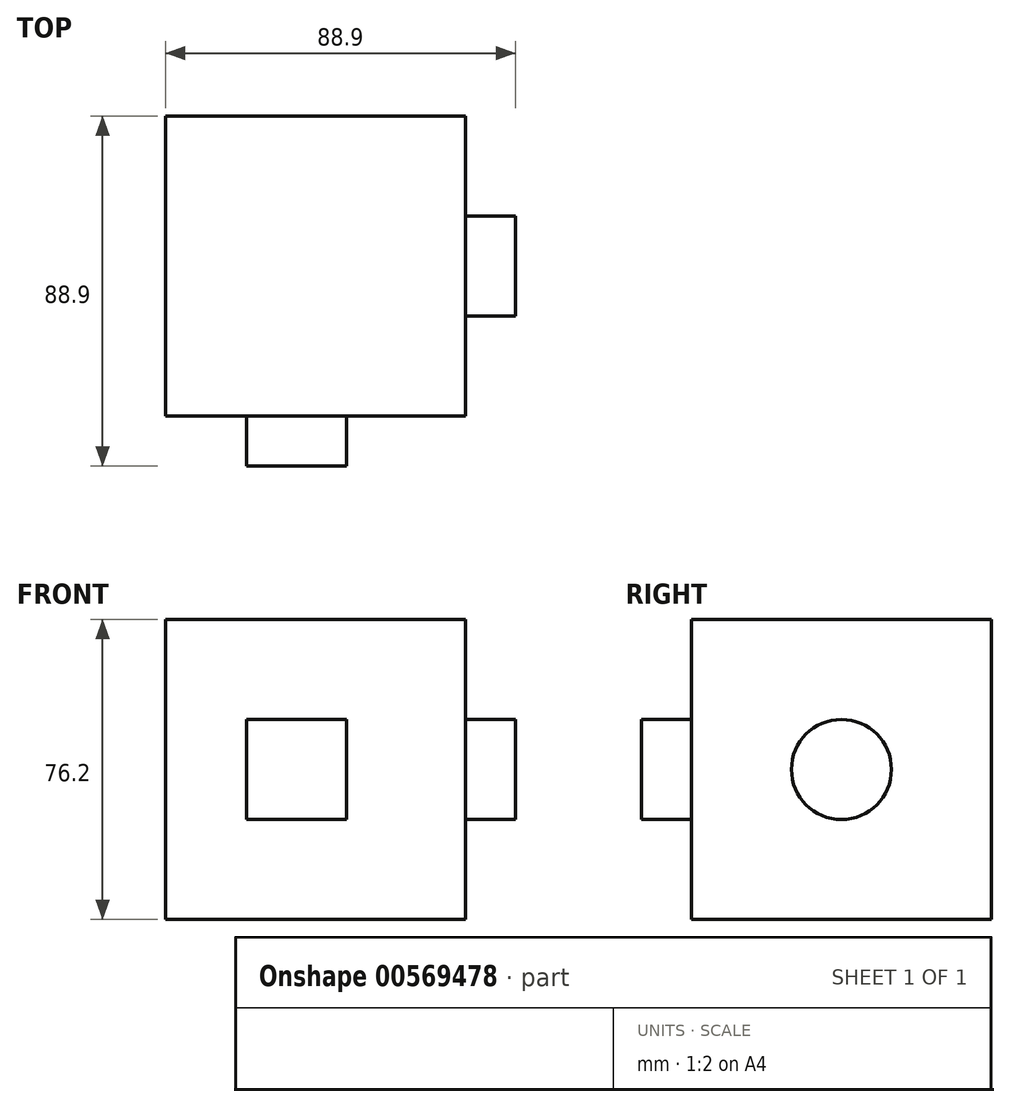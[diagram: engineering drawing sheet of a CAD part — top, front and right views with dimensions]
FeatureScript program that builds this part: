
annotation { "Feature Type Name" : "Feature", "Feature Type Description" : "" }
export const myFeature = defineFeature(function(context is Context, id is Id, definition is map)
    precondition{}
    {
        {
            var Q0;
            Q0=qCreatedBy(makeId("Front.planeOp"),FACE);
            var sketch = newSketch(context, id + "F0", { "sketchPlane" : qUnion([Q0])});
            skLineSegment(sketch, "E0.bottom", {"start": v(-1.68, 93.92) * mm, "end": v(74.52, 93.92) * mm});
            skLineSegment(sketch, "E0.top", {"start": v(-1.68, 17.72) * mm, "end": v(74.52, 17.72) * mm});
            skLineSegment(sketch, "E0.left", {"start": v(-1.68, 93.92) * mm, "end": v(-1.68, 17.72) * mm});
            skLineSegment(sketch, "E0.right", {"start": v(74.52, 93.92) * mm, "end": v(74.52, 17.72) * mm});
            skSolve(sketch);
        }
        {
            var Q0;
            Q0=makeQuery(id+"F0.imprint","IMPRINT",FACE,{"disambiguationData":[TD([[makeQuery(id+"F0.imprint","IMPRINT",EDGE,{"derivedFrom":sQuery(id+"F0.wireOp",EDGE,"E0.bottom")}),-1.0]])]});
            extrude(context, id + "F1", {"entities" : qUnion([Q0]), "depth" : 76.2 * mm, "offsetDistance" : 25.4 * mm});
        }
        {
            var Q0;
            Q0=makeQuery(id+"F1.opExtrude","CAP_FACE",FACE,{"disambiguationData":[OSD([sQuery(id+"F0.wireOp",EDGE,"E0.bottom"),sQuery(id+"F0.wireOp",EDGE,"E0.top"),sQuery(id+"F0.wireOp",EDGE,"E0.left"),sQuery(id+"F0.wireOp",EDGE,"E0.right")])],"isStart":false});
            var sketch = newSketch(context, id + "F2", { "sketchPlane" : qUnion([Q0])});
            skLineSegment(sketch, "E1.bottom", {"start": v(18.84, 68.52) * mm, "end": v(44.24, 68.52) * mm});
            skLineSegment(sketch, "E1.top", {"start": v(18.84, 43.12) * mm, "end": v(44.24, 43.12) * mm});
            skLineSegment(sketch, "E1.left", {"start": v(18.84, 68.52) * mm, "end": v(18.84, 43.12) * mm});
            skLineSegment(sketch, "E1.right", {"start": v(44.24, 68.52) * mm, "end": v(44.24, 43.12) * mm});
            skSolve(sketch);
        }
        {
            var Q0;
            Q0=makeQuery(id+"F2.imprint","IMPRINT",FACE,{"disambiguationData":[TD([[makeQuery(id+"F2.imprint","IMPRINT",EDGE,{"derivedFrom":sQuery(id+"F2.wireOp",EDGE,"E1.bottom")}),-1.0]])]});
            extrude(context, id + "F3", {"entities" : qUnion([Q0]), "operationType" : NewBodyOperationType.ADD, "depth" : 12.7 * mm, "offsetDistance" : 25.4 * mm});
        }
        {
            var Q0;
            Q0=makeQuery(id+"F1.opExtrude","SWEPT_FACE",FACE,{"disambiguationData":[OSD([sQuery(id+"F0.wireOp",EDGE,"E0.right")])]});
            var sketch = newSketch(context, id + "F4", { "sketchPlane" : qUnion([Q0])});
            skCircle(sketch, "E2", {"center": v(-38.1, 55.82) * mm, "radius": 12.7 * mm});
            skSolve(sketch);
        }
        {
            var Q0;
            Q0 = qSketchRegion(id + "F4", true);
            extrude(context, id + "F5", {"entities" : qUnion([Q0]), "operationType" : NewBodyOperationType.ADD, "depth" : 12.7 * mm, "offsetDistance" : 25.4 * mm});
        }
    });
